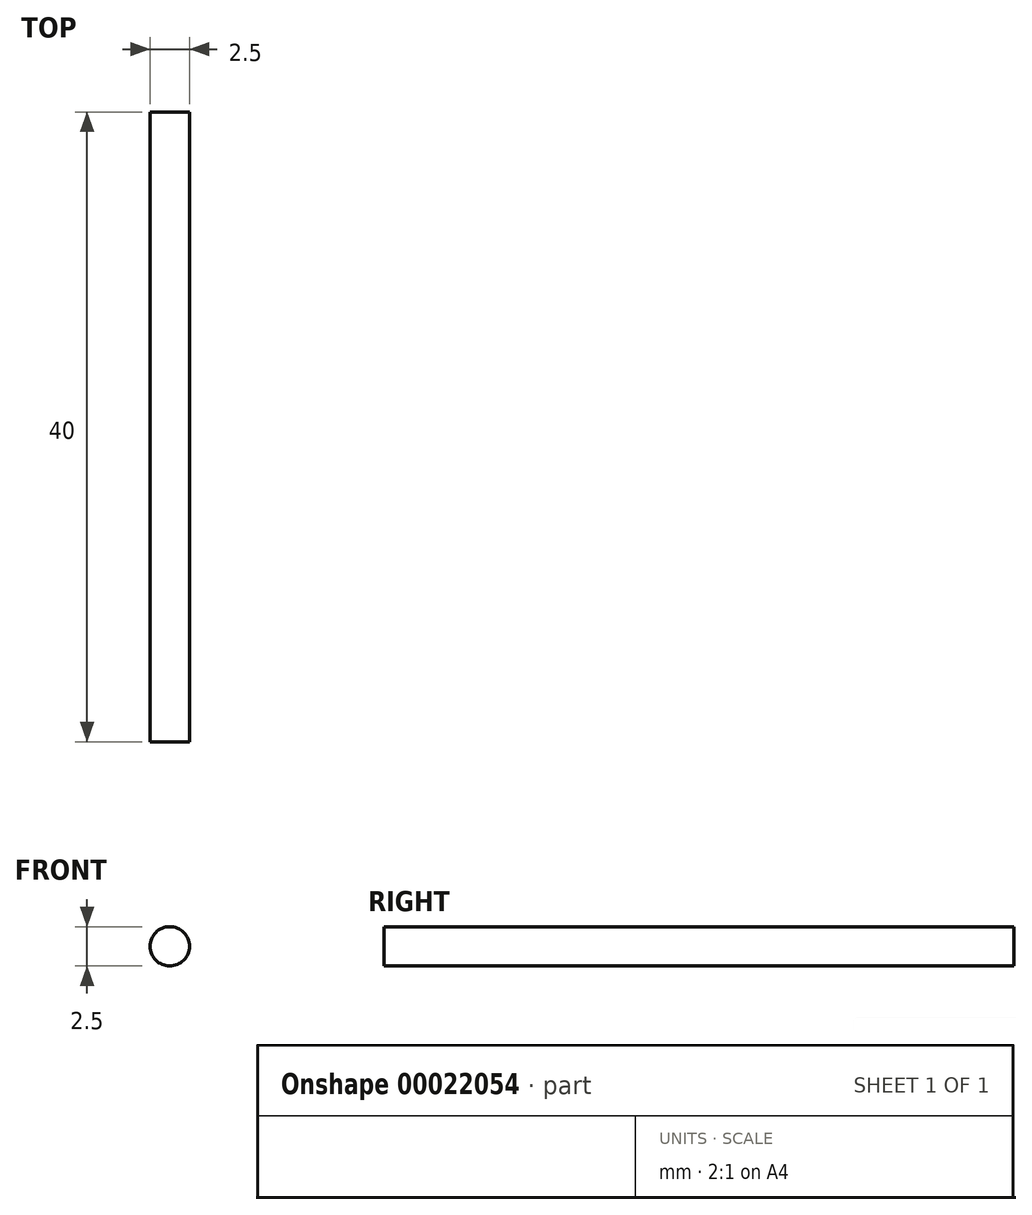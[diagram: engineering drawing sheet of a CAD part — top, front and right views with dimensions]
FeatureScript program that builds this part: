
annotation { "Feature Type Name" : "Feature", "Feature Type Description" : "" }
export const myFeature = defineFeature(function(context is Context, id is Id, definition is map)
    precondition{}
    {
        {
            var Q0;
            Q0=qCreatedBy(makeId("Front.planeOp"),FACE);
            var sketch = newSketch(context, id + "F0", { "sketchPlane" : qUnion([Q0])});
            skCircle(sketch, "E0", {"center": v(-17.88, 24.58) * mm, "radius": 1.25 * mm});
            skSolve(sketch);
        }
        {
            var Q0;
            Q0=makeQuery(id+"F0.imprint","IMPRINT",FACE,{"disambiguationData":[TD([[makeQuery(id+"F0.imprint","IMPRINT",EDGE,{"derivedFrom":sQuery(id+"F0.wireOp",EDGE,"E0")}),1.0]])]});
            extrude(context, id + "F1", {"entities" : qUnion([Q0]), "depth" : 40 * mm});
        }
    });
